# Revit family: PRD_AR_ShwrFttngsPckg_F5EShowerPanel_F3SV2012
name_source: partatom
category: Plumbing Fixtures
units: mm (PartAtom-declared; Revit-internal decimal feet)

## family parameters
Cut with Voids When Loaded = No
Enable Cutting in Views = No
Host = Face
Maintain Annotation Orientation = No
OmniClass Number = 23.45.05.14.17.11
OmniClass Title = Shower Compartments
Part Type = Normal
Room Calculation Point = No
Round Connector Dimension = Use Diameter
Shared = No

## types (1)
- F3SV2012
    AccentColour = chrome-look (glossy)
    AdditionalConnections = No
    AdjustableFlowTime = Yes
    Adjustment = Yes
    AssetType = Fixed
    BIMObjectName = PRD_AR_ ShowerFittingsPackage_F3SShowerPanel_F3SV2012
    BasicColour = stainless steel-look
    BodyMaterial = PRD_AR_StainlessSteel_SatinFinished
    Category = Pr_40_20_87_75, Shower fittings package
    Circulation = No
    Color = stainless steel-look
    CompatibleA3000Open = No
    ConnectionWithPayWaterDispenser = not possible
    DN = 15  [stored 0.0492126 ft]
    Default Elevation = 1200 mm
    Description = F3S shower panel made of stainless steel for wall mounting with DN 15 self-closing straight-way valve and connecting nozzles for shower head. Especially suitable for facilities at risk of vandalism. Hydraulically controlled, for connection from the rear to pre-mixed hot or cold water. Self-closing functional part, piston-free design, self-closing and stepless adjustment of flow duration. Valve housing including shuttle valve seat, visible parts polished chromium-plated.  Connecting nozzles for the required additional DN 15 KWC shower head with pre-fitted flow regulator 9.0 l/min. Housing made of stainless steel, single-piece enclosed, including safety screws. Connecting hose with lockable water flow regulator and strainer.
    DiameterNominal = DN 15
    DrainSize = 15 mm  [stored 0.0492126 ft]
    Export Type to IFC As = IfcSanitaryTerminalType
    Features = For connection from the rear to pre-mixed hot or cold water. Visible parts polished chromium-plated. Housing dimensions 232 x 1160 x 90 mm. Shower head must be ordered separately.
    Finish = satin finished
    Flow = 0.2 L/s
    ForHandShower = No
    FunctionalPrinciple = Hydraulic self-closing
    HasTray = No
    HygieneFlushing = No
    IfcExportAs = IfcSanitaryTerminalType
    IfcExportType = SHOWER
    InletSize = G 1/2 A
    LockingMechanism = Top section, ceramic
    Manufacturer = KWC Group Management AG
    ManufacturerName = KWC Group Management AG
    ManufacturerURL = www.kwc-professional.com
    Material = stainless steel
    MaterialCasing = stainless steel
    MaterialCodeCasing = 1.4301 Chrome Nickel steel V2A
    MaterialFitting = brass-look
    MaximumFlowTime = 35 Seconds
    MinimumFlowPressure = 1.5 bar
    MinimumFlowTime = 5 Seconds
    Model = F3SV2012
    ModelNumber = 2030070435
    ModelReference = F3SV2012
    NBSDescription = Shower fittings package
    NBSReference = 45-35-70/330
    Name = F3S Shower panel F3SV2012
    NominalDepth = 90 mm  [stored 0.295276 ft]
    NominalHeight = 1160 mm  [stored 3.80577 ft]
    NominalLength = 1160 mm  [stored 3.80577 ft]
    NominalWidth = 232 mm  [stored 0.761155 ft]
    OverallDepth = 90 mm
    OverallHeight = 1160 mm
    OverallWidth = 232 mm
    PositionOfWaterConnection = from top / backside
    ProductInformation = http://pim.kwc.com
    ProtectiveShutdown = No
    Push-button = No
    ShowerHead = for separately shower head
    ShowerPipeDraining = No
    ShowerType = Individual
    Size = 15
    SoundInsulation = No
    Status = NEW
    SurfaceFinishCasing = satin finished
    SurfaceFinishFitting = chromed
    SurfaceTreatmentFitting = polished
    TemperatureLimit = No
    ThermalDisinfection = No
    Type IFC Predefined Type = SHOWER
    TypeOfMixing = No
    TypeOfMounting = wall mounting
    TypeOfOperation = manual operation
    TypeOfShower = shower panel
    URL = www.kwc-professional.com
    Uniclass2015Code = Pr_40_20_87_75
    Uniclass2015Title = Shower fittings package
    Uniclass2015Version = Products v1.36
    Version = 1
    VolumeFlowRateAt3Bar = 0.15 l/s
    WaterConnection = hose (gland nut)
    WithBackflowPreventer = Yes
    WithFilter = Yes
    WithRosettesCoverPlate = Yes
    WithShowerSet = No
    WithSoapDish = No

note: [stored X ft] marks values corroborated as IEEE doubles in the binary element streams (Revit-internal decimal feet)

## geometry (parser evidence)
native form markers: Sweep x5
no freeform markers — native parametric forms only
